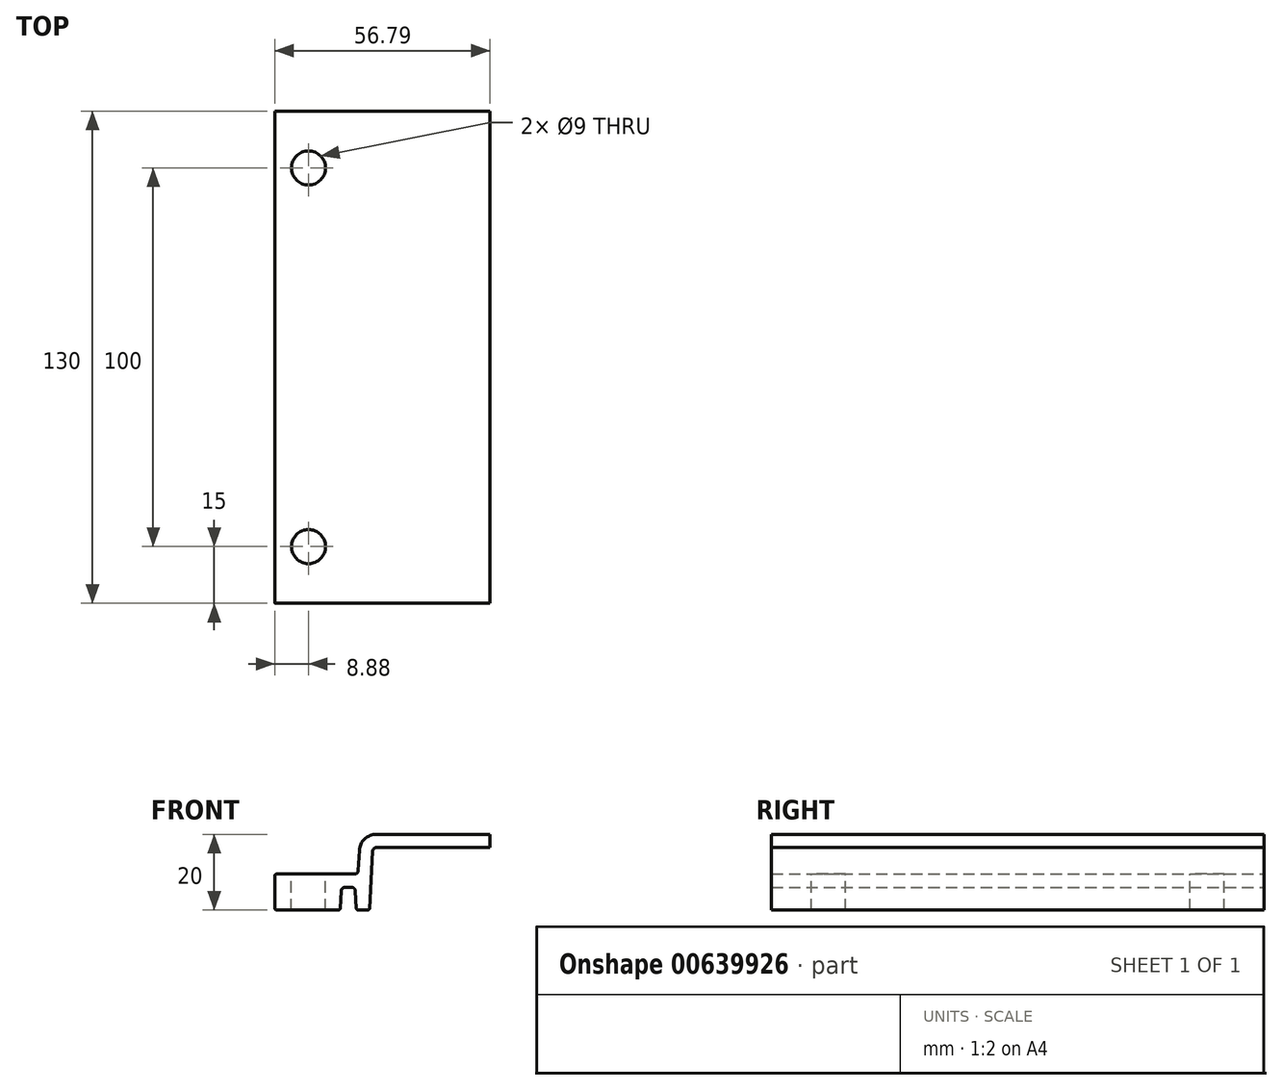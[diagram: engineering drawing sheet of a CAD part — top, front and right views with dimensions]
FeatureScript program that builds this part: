
annotation { "Feature Type Name" : "Feature", "Feature Type Description" : "" }
export const myFeature = defineFeature(function(context is Context, id is Id, definition is map)
    precondition{}
    {
        {
            var Q0;
            Q0=qCreatedBy(makeId("Front.planeOp"),FACE);
            var sketch = newSketch(context, id + "F0", { "sketchPlane" : qUnion([Q0])});
            skLineSegment(sketch, "E0", {"start": v(0, 0) * mm, "end": v(0, 8.5) * mm});
            skArc(sketch, "E1", {"start": v(0.5, 9) * mm, "mid": v(0.15, 8.85) * mm, "end": v(0, 8.5) * mm});
            skLineSegment(sketch, "E2", {"start": v(0.5, 9) * mm, "end": v(21.02, 9) * mm});
            skArc(sketch, "E3", {"start": v(21.02, 9) * mm, "mid": v(21.7, 9.27) * mm, "end": v(22.02, 9.95) * mm});
            skLineSegment(sketch, "E4", {"start": v(22.02, 9.95) * mm, "end": v(22.3, 15.24) * mm});
            skArc(sketch, "E5", {"start": v(26.79, 19.5) * mm, "mid": v(23.7, 18.26) * mm, "end": v(22.3, 15.24) * mm});
            skLineSegment(sketch, "E6", {"start": v(26.79, 19.5) * mm, "end": v(56.79, 19.5) * mm});
            skLineSegment(sketch, "E7", {"start": v(56.79, 19.5) * mm, "end": v(56.79, 16) * mm});
            skLineSegment(sketch, "E8", {"start": v(56.79, 16) * mm, "end": v(26.79, 16) * mm});
            skArc(sketch, "E9", {"start": v(26.79, 16) * mm, "mid": v(26.1, 15.73) * mm, "end": v(25.8, 15.05) * mm});
            skLineSegment(sketch, "E10", {"start": v(25.8, 15.05) * mm, "end": v(25, -0.03) * mm});
            skArc(sketch, "E11", {"start": v(24.5, -0.5) * mm, "mid": v(24.84, -0.36) * mm, "end": v(25, -0.03) * mm});
            skLineSegment(sketch, "E12", {"start": v(24.5, -0.5) * mm, "end": v(22, -0.5) * mm});
            skArc(sketch, "E13", {"start": v(21.5, -0.03) * mm, "mid": v(21.66, -0.36) * mm, "end": v(22, -0.5) * mm});
            skLineSegment(sketch, "E14", {"start": v(21.5, -0.03) * mm, "end": v(21.26, 4.55) * mm});
            skArc(sketch, "E15", {"start": v(21.26, 4.55) * mm, "mid": v(20.95, 5.23) * mm, "end": v(20.26, 5.5) * mm});
            skLineSegment(sketch, "E16", {"start": v(20.26, 5.5) * mm, "end": v(18.5, 5.5) * mm});
            skArc(sketch, "E17", {"start": v(18.5, 5.5) * mm, "mid": v(17.81, 5.23) * mm, "end": v(17.5, 4.55) * mm});
            skLineSegment(sketch, "E18", {"start": v(17.5, 4.55) * mm, "end": v(17.26, -0.03) * mm});
            skArc(sketch, "E19", {"start": v(16.76, -0.5) * mm, "mid": v(17.1, -0.36) * mm, "end": v(17.26, -0.03) * mm});
            skLineSegment(sketch, "E20", {"start": v(16.76, -0.5) * mm, "end": v(0.5, -0.5) * mm});
            skArc(sketch, "E21", {"start": v(0, 0) * mm, "mid": v(0.15, -0.35) * mm, "end": v(0.5, -0.5) * mm});
            skLineSegment(sketch, "E22", {"start": v(26.79, 19.5) * mm, "end": v(26.79, 16) * mm, "construction": true});
            skSolve(sketch);
        }
        {
            var Q0;
            Q0 = qSketchRegion(id + "F0", true);
            extrude(context, id + "F1", {"entities" : qUnion([Q0]), "depth" : 130 * mm, "offsetDistance" : 25 * mm});
        }
        {
            var Q0;
            Q0=makeQuery(id+"F1.opExtrude","SWEPT_FACE",FACE,{"disambiguationData":[OSD([sQuery(id+"F0.wireOp",EDGE,"E2")])]});
            var sketch = newSketch(context, id + "F2", { "sketchPlane" : qUnion([Q0])});
            skPoint(sketch, "E23", {"position": v(8.88, -15) * mm});
            skPoint(sketch, "E24", {"position": v(8.88, -115) * mm});
            skLineSegment(sketch, "E25", {"start": v(8.88, -15) * mm, "end": v(8.88, -115) * mm, "construction": true});
            skSolve(sketch);
        }
        {
            var Q0;
            Q0=sQuery(id+"F2.wireOp",VERTEX,"E23");
            var Q1;
            Q1=makeQuery(id+"F1.opExtrude","SWEPT_BODY",BODY,{"disambiguationData":[OSD([sQuery(id+"F0.wireOp",EDGE,"E0"),sQuery(id+"F0.wireOp",EDGE,"E1"),sQuery(id+"F0.wireOp",EDGE,"E2"),sQuery(id+"F0.wireOp",EDGE,"E3"),sQuery(id+"F0.wireOp",EDGE,"E4"),sQuery(id+"F0.wireOp",EDGE,"E5"),sQuery(id+"F0.wireOp",EDGE,"E6"),sQuery(id+"F0.wireOp",EDGE,"E7"),sQuery(id+"F0.wireOp",EDGE,"E8"),sQuery(id+"F0.wireOp",EDGE,"E9"),sQuery(id+"F0.wireOp",EDGE,"E10"),sQuery(id+"F0.wireOp",EDGE,"E11"),sQuery(id+"F0.wireOp",EDGE,"E12"),sQuery(id+"F0.wireOp",EDGE,"E13"),sQuery(id+"F0.wireOp",EDGE,"E14"),sQuery(id+"F0.wireOp",EDGE,"E15"),sQuery(id+"F0.wireOp",EDGE,"E16"),sQuery(id+"F0.wireOp",EDGE,"E17"),sQuery(id+"F0.wireOp",EDGE,"E18"),sQuery(id+"F0.wireOp",EDGE,"E19"),sQuery(id+"F0.wireOp",EDGE,"E20"),sQuery(id+"F0.wireOp",EDGE,"E21")])]});
            hole(context, id + "F3", {"style" : HoleStyle.SIMPLE, "endStyle" : HoleEndStyle.THROUGH, "holeDiameter" : 9 * mm, "majorDiameter" : 5 * mm, "isTappedThrough" : true, "tappedDepth" : 12 * mm, "tapClearance" : 3, "locations" : qUnion([Q0]), "scope" : qUnion([Q1])});
        }
        {
            var Q0;
            Q0=sQuery(id+"F2.wireOp",VERTEX,"E24");
            var Q1;
            Q1=makeQuery(id+"F1.opExtrude","SWEPT_BODY",BODY,{"disambiguationData":[OSD([sQuery(id+"F0.wireOp",EDGE,"E0"),sQuery(id+"F0.wireOp",EDGE,"E1"),sQuery(id+"F0.wireOp",EDGE,"E2"),sQuery(id+"F0.wireOp",EDGE,"E3"),sQuery(id+"F0.wireOp",EDGE,"E4"),sQuery(id+"F0.wireOp",EDGE,"E5"),sQuery(id+"F0.wireOp",EDGE,"E6"),sQuery(id+"F0.wireOp",EDGE,"E7"),sQuery(id+"F0.wireOp",EDGE,"E8"),sQuery(id+"F0.wireOp",EDGE,"E9"),sQuery(id+"F0.wireOp",EDGE,"E10"),sQuery(id+"F0.wireOp",EDGE,"E11"),sQuery(id+"F0.wireOp",EDGE,"E12"),sQuery(id+"F0.wireOp",EDGE,"E13"),sQuery(id+"F0.wireOp",EDGE,"E14"),sQuery(id+"F0.wireOp",EDGE,"E15"),sQuery(id+"F0.wireOp",EDGE,"E16"),sQuery(id+"F0.wireOp",EDGE,"E17"),sQuery(id+"F0.wireOp",EDGE,"E18"),sQuery(id+"F0.wireOp",EDGE,"E19"),sQuery(id+"F0.wireOp",EDGE,"E20"),sQuery(id+"F0.wireOp",EDGE,"E21")])]});
            hole(context, id + "F4", {"style" : HoleStyle.SIMPLE, "endStyle" : HoleEndStyle.THROUGH, "holeDiameter" : 9 * mm, "majorDiameter" : 5 * mm, "isTappedThrough" : true, "tappedDepth" : 12 * mm, "tapClearance" : 3, "locations" : qUnion([Q0]), "scope" : qUnion([Q1])});
        }
    });
